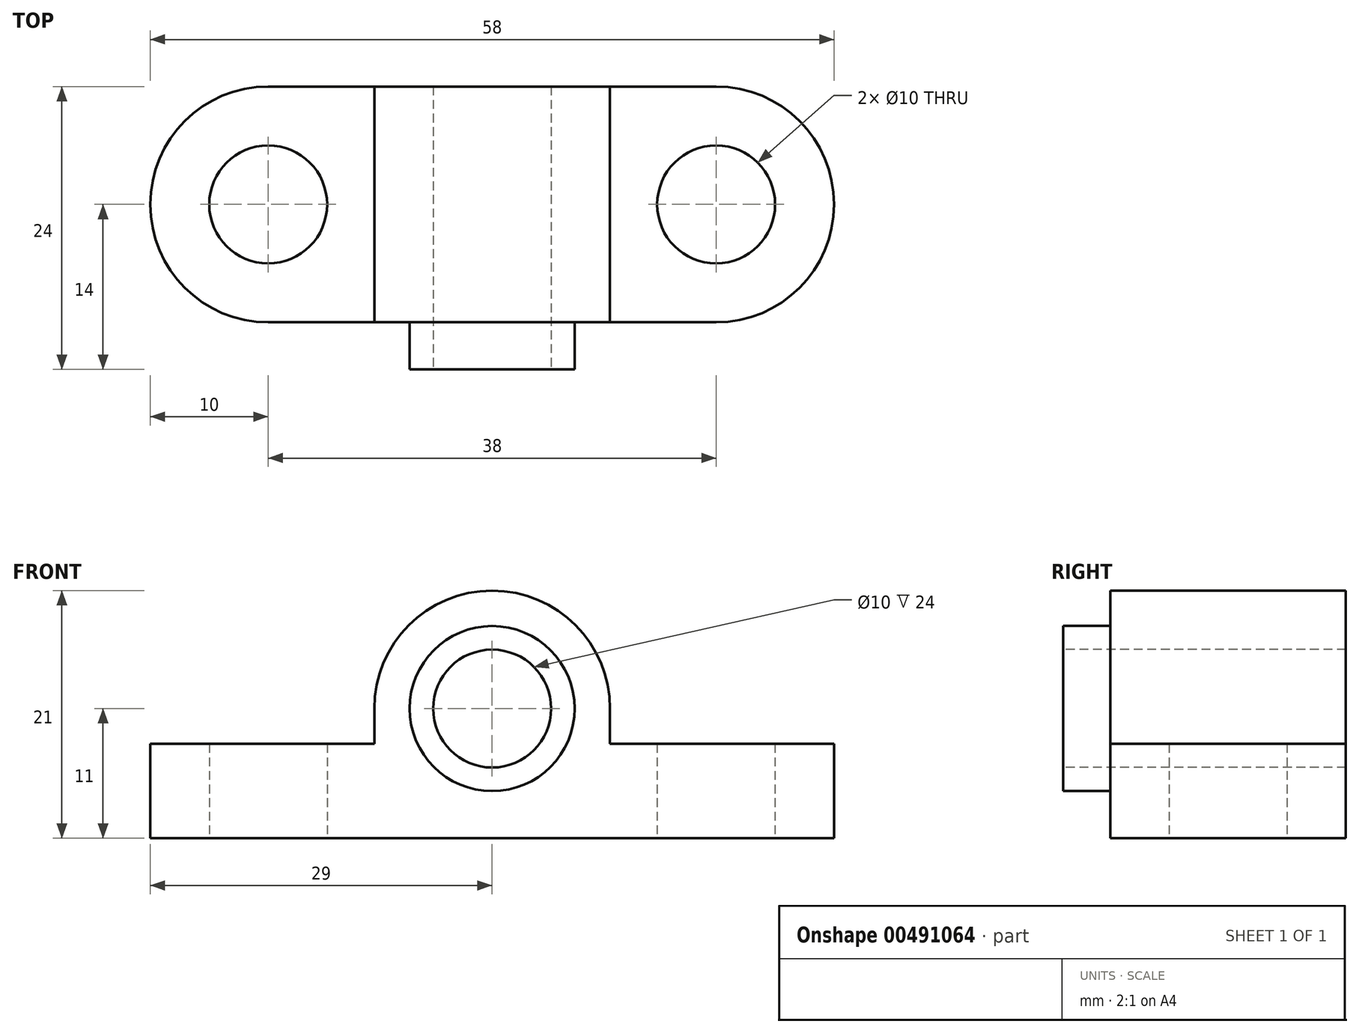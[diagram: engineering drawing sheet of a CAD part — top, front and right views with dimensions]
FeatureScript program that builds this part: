
annotation { "Feature Type Name" : "Feature", "Feature Type Description" : "" }
export const myFeature = defineFeature(function(context is Context, id is Id, definition is map)
    precondition{}
    {
        {
            var Q0;
            Q0=qCreatedBy(makeId("Top.planeOp"),FACE);
            var sketch = newSketch(context, id + "F0", { "sketchPlane" : qUnion([Q0])});
            skLineSegment(sketch, "E0.bottom", {"start": v(19, -10) * mm, "end": v(-19, -10) * mm});
            skLineSegment(sketch, "E0.top", {"start": v(19, 10) * mm, "end": v(-19, 10) * mm});
            skPoint(sketch, "E0.middle", {"position": v(0, 0) * mm});
            skArc(sketch, "E1", {"start": v(-19, 10) * mm, "mid": v(-29, 0) * mm, "end": v(-19, -10) * mm});
            skArc(sketch, "E2", {"start": v(19, -10) * mm, "mid": v(29, 0) * mm, "end": v(19, 10) * mm});
            skCircle(sketch, "E3", {"center": v(-19, 0) * mm, "radius": 5 * mm});
            skCircle(sketch, "E4", {"center": v(19, 0) * mm, "radius": 5 * mm});
            skSolve(sketch);
        }
        {
            var Q0;
            Q0 = qSketchRegion(id + "F0", true);
            extrude(context, id + "F1", {"entities" : qUnion([Q0]), "depth" : 8 * mm});
        }
        {
            var Q0;
            Q0=makeQuery(id+"F1.opExtrude","SWEPT_FACE",FACE,{"disambiguationData":[OSD([sQuery(id+"F0.wireOp",EDGE,"E0.bottom")])]});
            var sketch = newSketch(context, id + "F2", { "sketchPlane" : qUnion([Q0])});
            skLineSegment(sketch, "E5", {"start": v(-10, 8) * mm, "end": v(-10, 11) * mm});
            skLineSegment(sketch, "E6", {"start": v(10, 8) * mm, "end": v(10, 11) * mm});
            skArc(sketch, "E7", {"start": v(10, 11) * mm, "mid": v(0, 21) * mm, "end": v(-10, 11) * mm});
            skCircle(sketch, "E8", {"center": v(0, 11) * mm, "radius": 7 * mm});
            skCircle(sketch, "E9", {"center": v(0, 11) * mm, "radius": 5 * mm});
            skSolve(sketch);
        }
        {
            var Q0;
            {var subQ5=sQuery(id+"F2.wireOp",EDGE,"E5");Q0=makeQuery(id+"F2.imprint","IMPRINT",FACE,{"disambiguationData":[TD([[makeQuery(id+"F2.imprint","IMPRINT",EDGE,{"derivedFrom":subQ5}),-1.0]])]});}
            var Q1;
            {var subQ0=sQuery(id+"F2.wireOp",EDGE,"E8");var subQ1=makeQuery(id+"F1.opExtrude","CAP_EDGE",EDGE,{"disambiguationData":[OSD([sQuery(id+"F0.wireOp",EDGE,"E0.bottom")])],"isStart":false});var subQ2=makeQuery(id+"F2.imprint","INTERSECT",VERTEX,{"disambiguationData":[OD(0.0)],"derivedFrom":[subQ1,subQ0]});Q1=makeQuery(id+"F2.imprint","IMPRINT",FACE,{"disambiguationData":[TD([[makeQuery(id+"F2.imprint","IMPRINT",EDGE,{"disambiguationData":[TD([[subQ2,1.0]])],"derivedFrom":subQ0}),1.0]])]});}
            var Q2;
            Q2=makeQuery(id+"F1.opExtrude","SWEPT_FACE",FACE,{"disambiguationData":[OSD([sQuery(id+"F0.wireOp",EDGE,"E0.top")])]});
            extrude(context, id + "F3", {"entities" : qUnion([Q0, Q1]), "operationType" : NewBodyOperationType.ADD, "endBound" : BoundingType.UP_TO_SURFACE, "oppositeDirection" : true, "endBoundEntityFace" : qUnion([Q2]), "depth" : 25 * mm});
        }
        {
            var Q0;
            {var subQ0=sQuery(id+"F2.wireOp",EDGE,"E9");var subQ1=makeQuery(id+"F1.opExtrude","CAP_EDGE",EDGE,{"disambiguationData":[OSD([sQuery(id+"F0.wireOp",EDGE,"E0.bottom")])],"isStart":false});var subQ2=makeQuery(id+"F2.imprint","INTERSECT",VERTEX,{"disambiguationData":[OD(0.0)],"derivedFrom":[subQ1,subQ0]});Q0=makeQuery(id+"F2.imprint","IMPRINT",FACE,{"disambiguationData":[TD([[makeQuery(id+"F2.imprint","IMPRINT",EDGE,{"disambiguationData":[TD([[subQ2,-1.0]])],"derivedFrom":subQ0}),1.0]])]});}
            extrude(context, id + "F4", {"entities" : qUnion([Q0]), "operationType" : NewBodyOperationType.REMOVE, "endBound" : BoundingType.THROUGH_ALL, "oppositeDirection" : true, "depth" : 25 * mm});
        }
        {
            var Q0;
            {var subQ0=sQuery(id+"F2.wireOp",EDGE,"E8");var subQ1=makeQuery(id+"F1.opExtrude","CAP_EDGE",EDGE,{"disambiguationData":[OSD([sQuery(id+"F0.wireOp",EDGE,"E0.bottom")])],"isStart":false});var subQ2=makeQuery(id+"F2.imprint","INTERSECT",VERTEX,{"disambiguationData":[OD(0.0)],"derivedFrom":[subQ1,subQ0]});Q0=makeQuery(id+"F2.imprint","IMPRINT",FACE,{"disambiguationData":[TD([[makeQuery(id+"F2.imprint","IMPRINT",EDGE,{"disambiguationData":[TD([[subQ2,1.0]])],"derivedFrom":subQ0}),1.0]])]});}
            var Q1;
            {var subQ0=sQuery(id+"F2.wireOp",EDGE,"E8");var subQ1=makeQuery(id+"F1.opExtrude","CAP_EDGE",EDGE,{"disambiguationData":[OSD([sQuery(id+"F0.wireOp",EDGE,"E0.bottom")])],"isStart":false});var subQ2=makeQuery(id+"F2.imprint","INTERSECT",VERTEX,{"disambiguationData":[OD(0.0)],"derivedFrom":[subQ1,subQ0]});Q1=makeQuery(id+"F2.imprint","IMPRINT",FACE,{"disambiguationData":[TD([[makeQuery(id+"F2.imprint","IMPRINT",EDGE,{"disambiguationData":[TD([[subQ2,-1.0]])],"derivedFrom":subQ0}),1.0]])]});}
            extrude(context, id + "F5", {"entities" : qUnion([Q0, Q1]), "operationType" : NewBodyOperationType.ADD, "depth" : 4 * mm});
        }
    });
